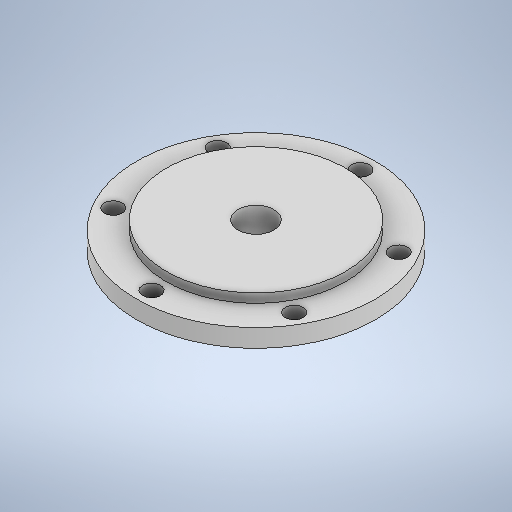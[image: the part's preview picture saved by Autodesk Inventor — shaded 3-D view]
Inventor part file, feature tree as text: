
AUTODESK INVENTOR PART (.ipt)
format: ipt  version: 2025.1 (Build 291241000, 241)  size: 287,744 bytes
history: native  units: mm
features: sketch x5, extrude x3, hole x2, pattern_circular x1, thread x1
ambient origin geometry x8: Origin, YZ Plane, XZ Plane, XY Plane, X Axis, Y Axis, Z Axis, Center Point
bodies: Solid1 (feature_tree)
feature tree (12):
  extrude  "Extrusion1"  Depth=3.0mm TaperAngle=0.0deg
  extrude  "Extrusion2"  Depth=1.5mm TaperAngle=0.0deg
  hole  "Hole1"  [1 undecoded]
  pattern_circular  "Circular Pattern1"  [2 undecoded]
  extrude  "Extrusion3"  Depth=6.0mm TaperAngle=0.0deg
  thread  "Thread1"  [1 undecoded]
  hole  "Hole5"  [1 undecoded]
  sketch  "Sketch1"  dims[d0=40.0mm d1=3.0mm d2=0.0mm]
  sketch  "Sketch2"  dims[d3=30.0mm d4=1.5mm d5=0.0mm]
  sketch  "Sketch3"  dims[d6=35.0mm]
  sketch  "Sketch4"  dims[d7=3.0mm d8=6.0mm d9=4.0mm d10=2.0mm d11=90.0deg d12=8.0mm d13=0.0mm d14=60.0mm d15=360.0deg]
  sketch  "Sketch8"  dims[d17=12.0mm d18=6.0mm d19=0.0mm d20=6.0mm d21=0.0mm d43=6.0mm d44=6.0mm d45=7.0mm d46=2.0mm d47=90.0deg d48=8.0mm d49=0.0mm]
note: 5 required parameter values undecoded (feature->parameter linkage not recoverable at this tier; creation-order binding heuristic only, values carry confidence <= 0.55)
